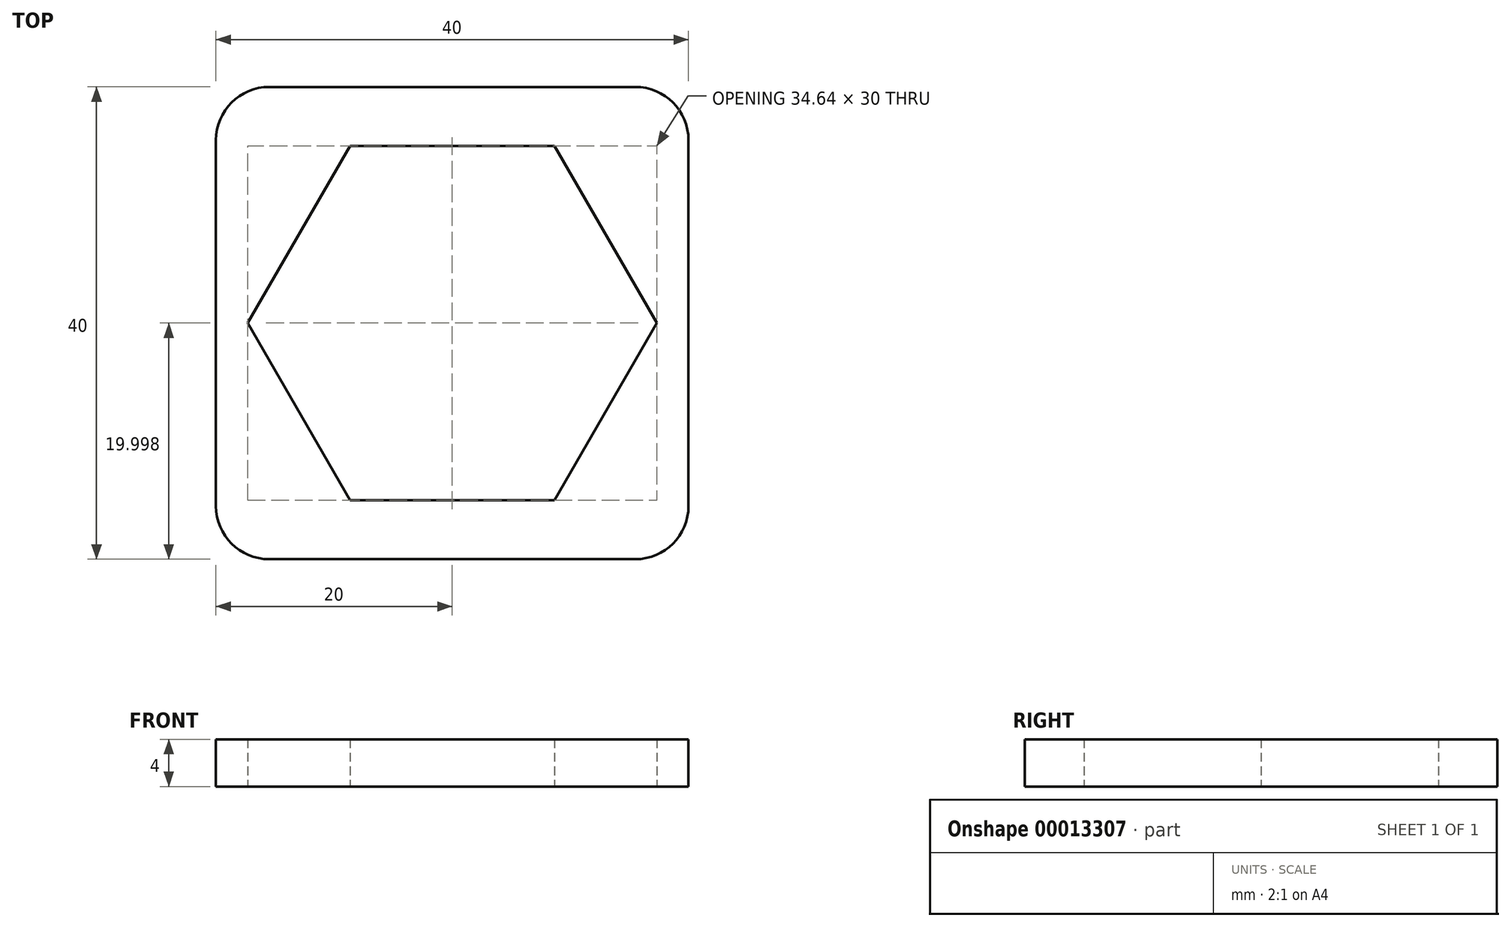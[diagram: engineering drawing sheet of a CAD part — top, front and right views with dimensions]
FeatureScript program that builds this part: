
annotation { "Feature Type Name" : "Feature", "Feature Type Description" : "" }
export const myFeature = defineFeature(function(context is Context, id is Id, definition is map)
    precondition{}
    {
        {
            var Q0;
            Q0=qCreatedBy(makeId("Top.planeOp"),FACE);
            var sketch = newSketch(context, id + "F0", { "sketchPlane" : qUnion([Q0])});
            skLineSegment(sketch, "E0.bottom", {"start": v(-17.27, 25.24) * mm, "end": v(13.73, 25.24) * mm});
            skLineSegment(sketch, "E0.top", {"start": v(-17.27, -14.76) * mm, "end": v(13.73, -14.76) * mm});
            skLineSegment(sketch, "E0.left", {"start": v(-21.77, 20.74) * mm, "end": v(-21.77, -10.26) * mm});
            skLineSegment(sketch, "E0.right", {"start": v(18.23, 20.74) * mm, "end": v(18.23, -10.26) * mm});
            skCircle(sketch, "E1.cCircle", {"center": v(-1.77, 5.24) * mm, "radius": 15 * mm, "construction": true});
            skLineSegment(sketch, "E1.0", {"start": v(6.9, -9.76) * mm, "end": v(-10.43, -9.76) * mm});
            skLineSegment(sketch, "E1.1", {"start": v(-10.43, -9.76) * mm, "end": v(-19.1, 5.24) * mm});
            skLineSegment(sketch, "E1.2", {"start": v(-19.1, 5.24) * mm, "end": v(-10.43, 20.24) * mm});
            skLineSegment(sketch, "E1.3", {"start": v(-10.43, 20.24) * mm, "end": v(6.9, 20.24) * mm});
            skLineSegment(sketch, "E1.4", {"start": v(6.9, 20.24) * mm, "end": v(15.55, 5.24) * mm});
            skLineSegment(sketch, "E1.5", {"start": v(15.55, 5.24) * mm, "end": v(6.9, -9.76) * mm});
            skPoint(sketch, "E1.0.midPoint", {"position": v(-1.77, -9.76) * mm});
            skPoint(sketch, "E2.visualSharp", {"position": v(-21.77, 25.24) * mm});
            skArc(sketch, "E2.filletArc", {"start": v(-17.27, 25.24) * mm, "mid": v(-20.45, 23.92) * mm, "end": v(-21.77, 20.74) * mm});
            skPoint(sketch, "E3.visualSharp", {"position": v(18.23, 25.24) * mm});
            skArc(sketch, "E3.filletArc", {"start": v(18.23, 20.74) * mm, "mid": v(16.91, 23.92) * mm, "end": v(13.73, 25.24) * mm});
            skPoint(sketch, "E4.visualSharp", {"position": v(18.23, -14.76) * mm});
            skArc(sketch, "E4.filletArc", {"start": v(13.73, -14.76) * mm, "mid": v(16.91, -13.44) * mm, "end": v(18.23, -10.26) * mm});
            skPoint(sketch, "E5.visualSharp", {"position": v(-21.77, -14.76) * mm});
            skArc(sketch, "E5.filletArc", {"start": v(-21.77, -10.26) * mm, "mid": v(-20.45, -13.44) * mm, "end": v(-17.27, -14.76) * mm});
            skSolve(sketch);
        }
        {
            var Q0;
            Q0 = qSketchRegion(id + "F0", true);
            extrude(context, id + "F1", {"entities" : qUnion([Q0]), "depth" : 4 * mm});
        }
    });
